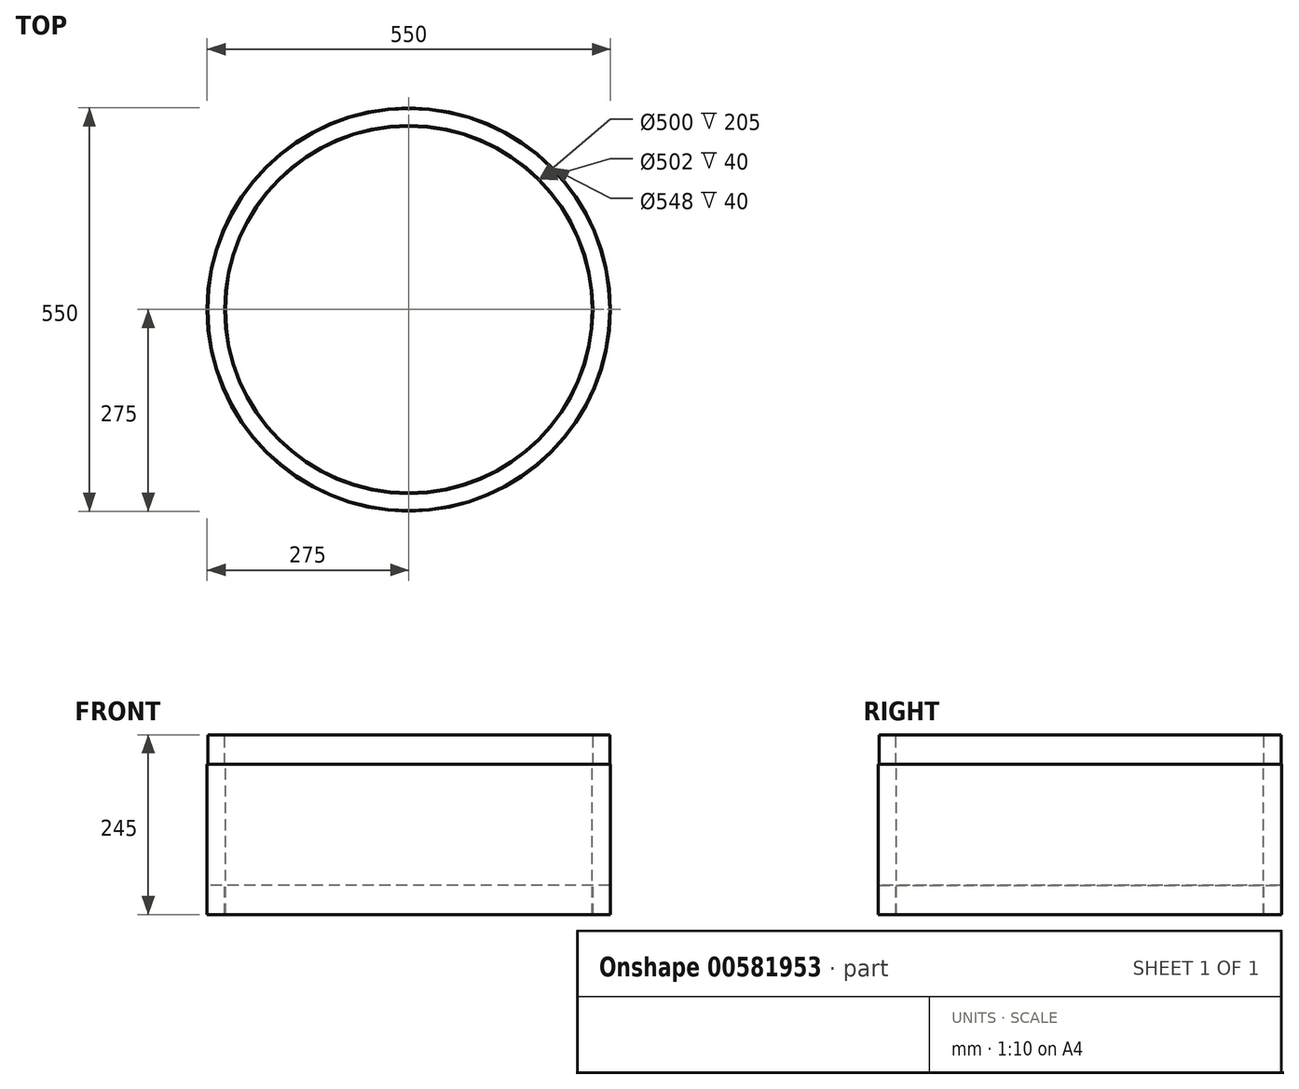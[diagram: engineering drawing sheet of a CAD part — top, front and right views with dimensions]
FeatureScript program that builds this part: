
annotation { "Feature Type Name" : "Feature", "Feature Type Description" : "" }
export const myFeature = defineFeature(function(context is Context, id is Id, definition is map)
    precondition{}
    {
        {
            var Q0;
            Q0=qCreatedBy(makeId("Front.planeOp"),FACE);
            var sketch = newSketch(context, id + "F0", { "sketchPlane" : qUnion([Q0])});
            skLineSegment(sketch, "E0", {"start": v(0, 345.75) * mm, "end": v(0, -558.03) * mm, "construction": true});
            skLineSegment(sketch, "E1", {"start": v(-250, -518.84) * mm, "end": v(-250, -313.84) * mm});
            skLineSegment(sketch, "E2", {"start": v(-250, -313.84) * mm, "end": v(-251, -313.84) * mm});
            skLineSegment(sketch, "E3", {"start": v(-251, -313.84) * mm, "end": v(-251, -273.84) * mm});
            skLineSegment(sketch, "E4", {"start": v(-251, -273.84) * mm, "end": v(-274, -273.84) * mm});
            skLineSegment(sketch, "E5", {"start": v(-274, -273.84) * mm, "end": v(-274, -313.84) * mm});
            skLineSegment(sketch, "E6", {"start": v(-274, -313.84) * mm, "end": v(-275, -313.84) * mm});
            skLineSegment(sketch, "E7", {"start": v(-275, -313.84) * mm, "end": v(-275, -518.84) * mm});
            skLineSegment(sketch, "E8", {"start": v(-275, -518.84) * mm, "end": v(-274, -518.84) * mm});
            skLineSegment(sketch, "E9", {"start": v(-274, -518.84) * mm, "end": v(-274, -478.84) * mm});
            skLineSegment(sketch, "E10", {"start": v(-274, -478.84) * mm, "end": v(-251, -478.84) * mm});
            skLineSegment(sketch, "E11", {"start": v(-251, -478.84) * mm, "end": v(-251, -518.84) * mm});
            skLineSegment(sketch, "E12", {"start": v(-251, -518.84) * mm, "end": v(-250, -518.84) * mm});
            skSolve(sketch);
        }
        {
            var Q0;
            Q0=qSketchRegion(id+"F0",true);
            var Q1;
            Q1=sQuery(id+"F0.wireOp",EDGE,"E0");
            revolve(context, id + "F1", {"entities" : qUnion([Q0]), "axis" : qUnion([Q1]), "revolveType" : RevolveType.FULL});
        }
    });
